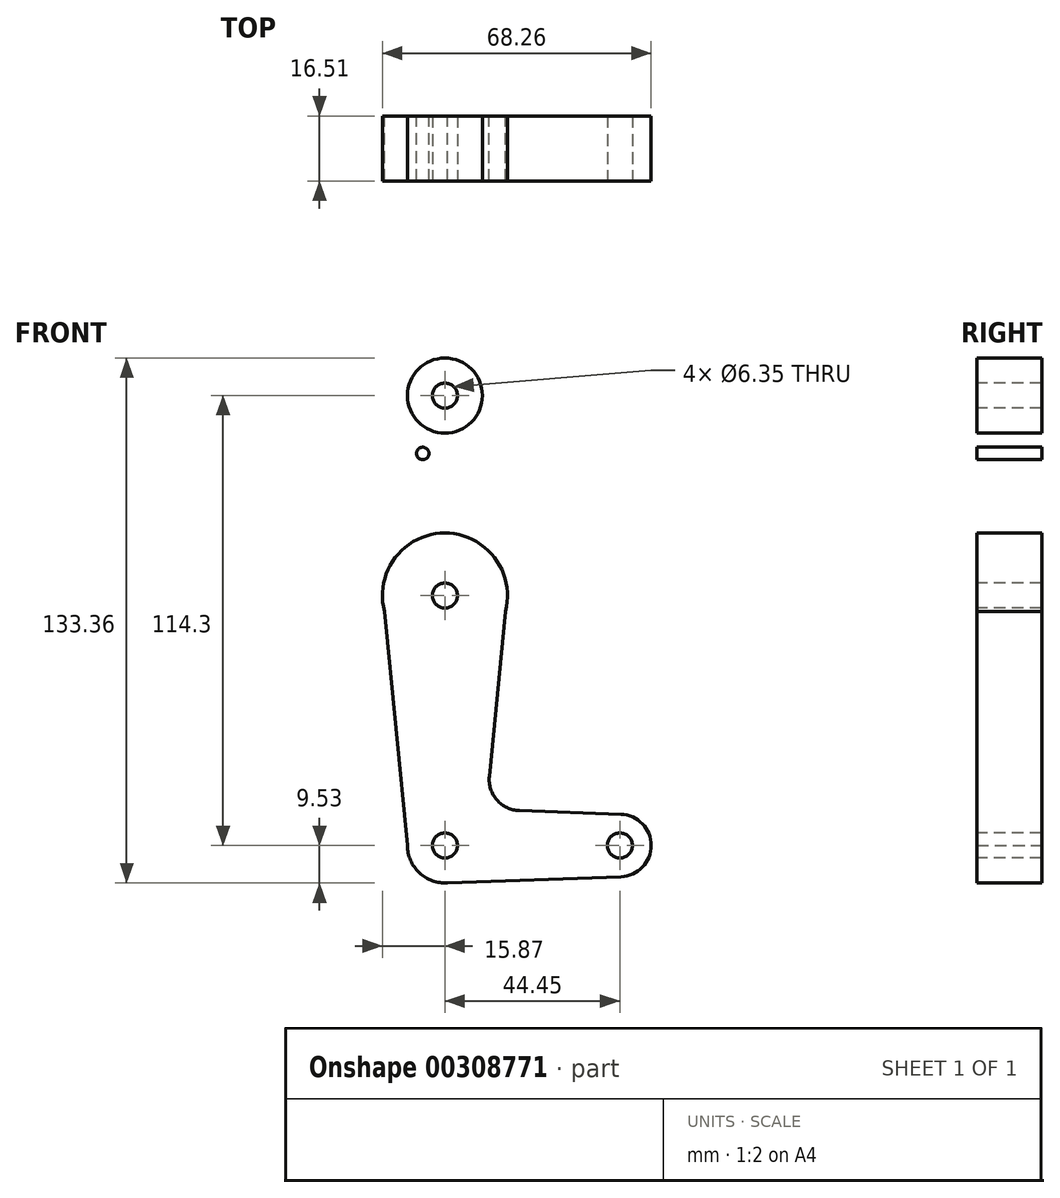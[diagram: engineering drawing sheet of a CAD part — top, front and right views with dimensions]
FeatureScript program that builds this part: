
annotation { "Feature Type Name" : "Feature", "Feature Type Description" : "" }
export const myFeature = defineFeature(function(context is Context, id is Id, definition is map)
    precondition{}
    {
        {
            var Q0;
            Q0=qCreatedBy(makeId("Front.planeOp"),FACE);
            var sketch = newSketch(context, id + "F0", { "sketchPlane" : qUnion([Q0])});
            skCircle(sketch, "E0", {"center": v(0, 50.8) * mm, "radius": 9.53 * mm});
            skCircle(sketch, "E1", {"center": v(0, 0) * mm, "radius": 15.88 * mm});
            skCircle(sketch, "E2", {"center": v(0, -63.5) * mm, "radius": 9.53 * mm});
            skCircle(sketch, "E3", {"center": v(44.45, -63.5) * mm, "radius": 7.94 * mm});
            skLineSegment(sketch, "E4", {"start": v(-15.35, -4.04) * mm, "end": v(-9.52, -63.5) * mm});
            skLineSegment(sketch, "E5", {"start": v(-9.52, -63.5) * mm, "end": v(-15.35, -4.04) * mm});
            skLineSegment(sketch, "E6", {"start": v(15.35, -4.04) * mm, "end": v(11.28, -45.93) * mm});
            skLineSegment(sketch, "E7", {"start": v(18.9, -54.65) * mm, "end": v(44.73, -55.57) * mm});
            skLineSegment(sketch, "E8", {"start": v(0, -73.02) * mm, "end": v(44.73, -71.43) * mm});
            skLineSegment(sketch, "E9", {"start": v(44.73, -71.43) * mm, "end": v(0, -73.02) * mm});
            skCircle(sketch, "E10", {"center": v(-5.63, 36.09) * mm, "radius": 1.59 * mm});
            skPoint(sketch, "E11.newPointA", {"position": v(9.57, -63.5) * mm});
            skArc(sketch, "E11.filletArc", {"start": v(11.28, -45.93) * mm, "mid": v(13.2, -51.94) * mm, "end": v(18.9, -54.65) * mm});
            skLineSegment(sketch, "E12", {"start": v(-15.74, 2.08) * mm, "end": v(-9.53, 50.8) * mm});
            skLineSegment(sketch, "E13", {"start": v(9.52, 50.8) * mm, "end": v(15.74, 2.08) * mm});
            skSolve(sketch);
        }
        {
            var Q0;
            Q0 = qSketchRegion(id + "F0", true);
            extrude(context, id + "F1", {"entities" : qUnion([Q0]), "depth" : 16.5 * mm});
        }
        {
            var Q0;
            Q0=makeQuery(id+"F1.opExtrude","CAP_FACE",FACE,{"disambiguationData":[OSD([sQuery(id+"F0.wireOp",EDGE,"E0"),sQuery(id+"F0.wireOp",EDGE,"E1"),sQuery(id+"F0.wireOp",EDGE,"E2"),sQuery(id+"F0.wireOp",EDGE,"E3"),sQuery(id+"F0.wireOp",EDGE,"E5"),sQuery(id+"F0.wireOp",EDGE,"E6"),sQuery(id+"F0.wireOp",EDGE,"E7"),sQuery(id+"F0.wireOp",EDGE,"E9"),sQuery(id+"F0.wireOp",EDGE,"E10"),sQuery(id+"F0.wireOp",EDGE,"E11.filletArc"),sQuery(id+"F0.wireOp",EDGE,"E12"),sQuery(id+"F0.wireOp",EDGE,"E13")])],"isStart":false});
            var sketch = newSketch(context, id + "F2", { "sketchPlane" : qUnion([Q0])});
            skCircle(sketch, "E14", {"center": v(0, 0) * mm, "radius": 3.18 * mm});
            skCircle(sketch, "E15", {"center": v(0, -63.5) * mm, "radius": 3.18 * mm});
            skCircle(sketch, "E16", {"center": v(44.45, -63.5) * mm, "radius": 3.18 * mm});
            skCircle(sketch, "E17", {"center": v(0, 50.8) * mm, "radius": 3.18 * mm});
            skSolve(sketch);
        }
        {
            var Q0;
            Q0 = qSketchRegion(id + "F2", true);
            extrude(context, id + "F3", {"entities" : qUnion([Q0]), "operationType" : NewBodyOperationType.REMOVE, "oppositeDirection" : true, "depth" : 60.96 * mm});
        }
    });
